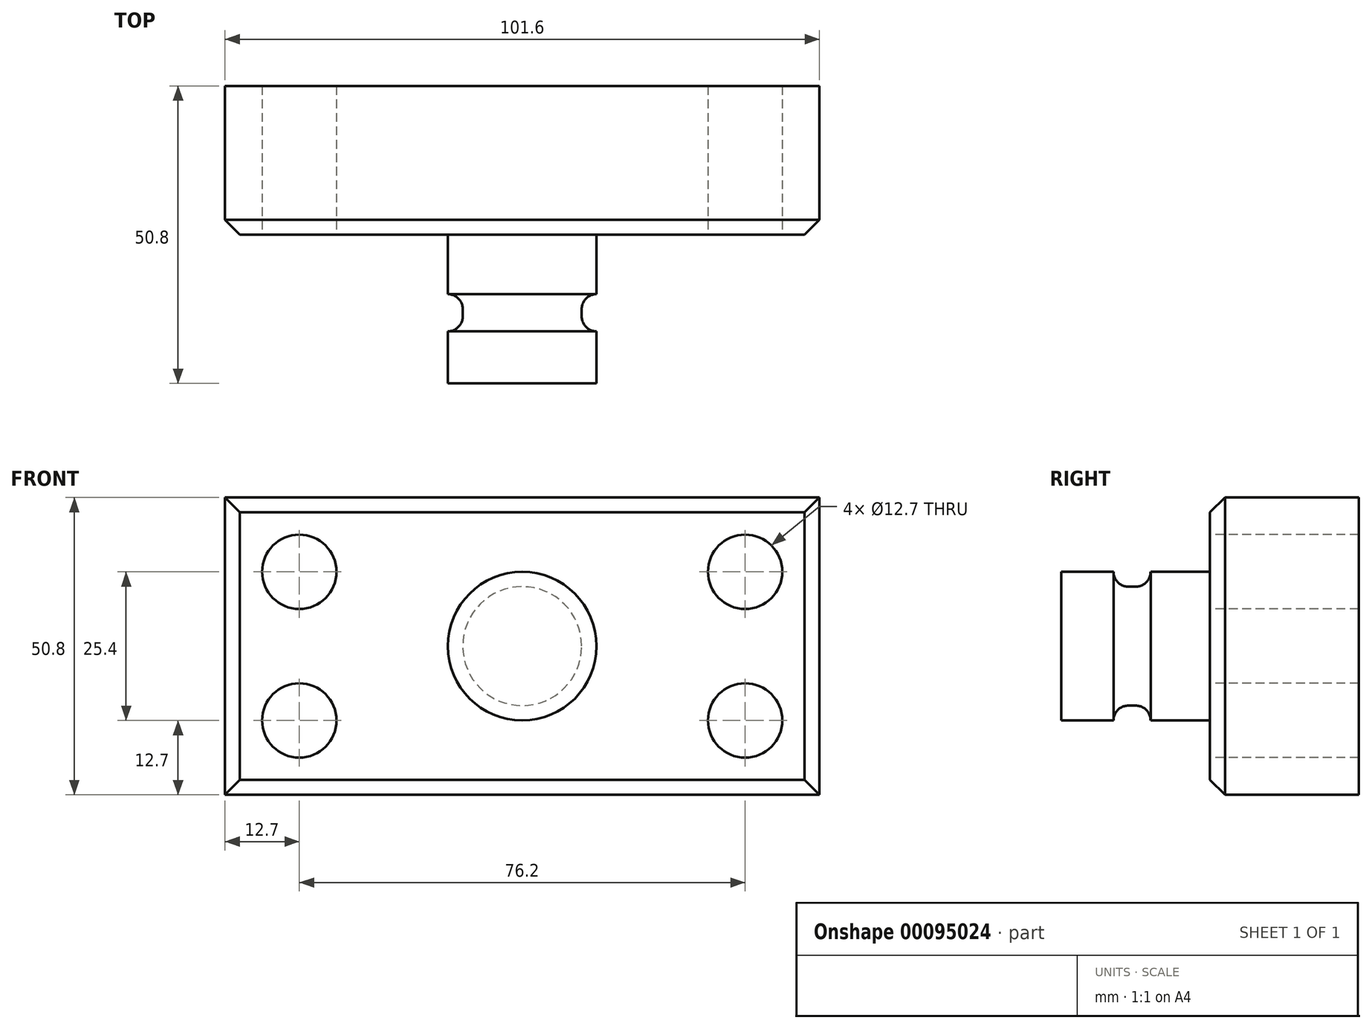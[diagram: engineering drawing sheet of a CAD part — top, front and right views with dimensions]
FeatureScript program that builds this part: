
annotation { "Feature Type Name" : "Feature", "Feature Type Description" : "" }
export const myFeature = defineFeature(function(context is Context, id is Id, definition is map)
    precondition{}
    {
        {
            var Q0;
            Q0=qCreatedBy(makeId("Front.planeOp"),FACE);
            var sketch = newSketch(context, id + "F0", { "sketchPlane" : qUnion([Q0])});
            skLineSegment(sketch, "E0.bottom", {"start": v(-50.8, 25.4) * mm, "end": v(50.8, 25.4) * mm});
            skLineSegment(sketch, "E0.top", {"start": v(-50.8, -25.4) * mm, "end": v(50.8, -25.4) * mm});
            skLineSegment(sketch, "E0.left", {"start": v(-50.8, 25.4) * mm, "end": v(-50.8, -25.4) * mm});
            skLineSegment(sketch, "E0.right", {"start": v(50.8, 25.4) * mm, "end": v(50.8, -25.4) * mm});
            skPoint(sketch, "E0.middle", {"position": v(0, 0) * mm});
            skSolve(sketch);
        }
        {
            var Q0;
            Q0=makeQuery(id+"F0.imprint","IMPRINT",FACE,{"disambiguationData":[TD([[makeQuery(id+"F0.imprint","IMPRINT",EDGE,{"derivedFrom":sQuery(id+"F0.wireOp",EDGE,"E0.bottom")}),-1.0]])]});
            extrude(context, id + "F1", {"entities" : qUnion([Q0]), "depth" : 25.4 * mm});
        }
        {
            var Q0;
            Q0=makeQuery(id+"F1.opExtrude","CAP_FACE",FACE,{"disambiguationData":[OSD([sQuery(id+"F0.wireOp",EDGE,"E0.bottom"),sQuery(id+"F0.wireOp",EDGE,"E0.top"),sQuery(id+"F0.wireOp",EDGE,"E0.left"),sQuery(id+"F0.wireOp",EDGE,"E0.right")])],"isStart":false});
            var sketch = newSketch(context, id + "F2", { "sketchPlane" : qUnion([Q0])});
            skCircle(sketch, "E1", {"center": v(-38.1, 12.7) * mm, "radius": 6.35 * mm});
            skCircle(sketch, "E2", {"center": v(-38.1, -12.7) * mm, "radius": 6.35 * mm});
            skCircle(sketch, "E3", {"center": v(38.1, 12.7) * mm, "radius": 6.35 * mm});
            skCircle(sketch, "E4", {"center": v(38.1, -12.7) * mm, "radius": 6.35 * mm});
            skSolve(sketch);
        }
        {
            var Q0;
            Q0 = qSketchRegion(id + "F2", true);
            extrude(context, id + "F3", {"entities" : qUnion([Q0]), "operationType" : NewBodyOperationType.REMOVE, "endBound" : BoundingType.THROUGH_ALL, "oppositeDirection" : true, "depth" : 25.4 * mm});
        }
        {
            var Q0;
            Q0=qCreatedBy(makeId("Top.planeOp"),FACE);
            var sketch = newSketch(context, id + "F4", { "sketchPlane" : qUnion([Q0])});
            skLineSegment(sketch, "E5.bottom", {"start": v(0, -25.4) * mm, "end": v(-12.7, -25.4) * mm});
            skLineSegment(sketch, "E5.top", {"start": v(0, -50.8) * mm, "end": v(-12.7, -50.8) * mm});
            skLineSegment(sketch, "E5.left", {"start": v(0, -25.4) * mm, "end": v(0, -50.8) * mm});
            skLineSegment(sketch, "E5.right", {"start": v(-12.7, -25.4) * mm, "end": v(-12.7, -50.8) * mm});
            skSolve(sketch);
        }
        {
            var Q0;
            Q0 = qSketchRegion(id + "F4", true);
            var Q1;
            Q1=sQuery(id+"F4.wireOp",EDGE,"E5.left");
            revolve(context, id + "F5", {"operationType" : NewBodyOperationType.ADD, "entities" : qUnion([Q0]), "axis" : qUnion([Q1]), "revolveType" : RevolveType.FULL});
        }
        {
            var Q0;
            Q0=qCreatedBy(makeId("Top.planeOp"),FACE);
            var sketch = newSketch(context, id + "F6", { "sketchPlane" : qUnion([Q0])});
            skLineSegment(sketch, "E6.bottom", {"start": v(-20.32, -41.91) * mm, "end": v(-10.16, -41.91) * mm});
            skLineSegment(sketch, "E6.top", {"start": v(-20.32, -35.56) * mm, "end": v(-10.16, -35.56) * mm});
            skLineSegment(sketch, "E6.left", {"start": v(-20.32, -41.91) * mm, "end": v(-20.32, -35.56) * mm});
            skLineSegment(sketch, "E6.right", {"start": v(-10.16, -41.91) * mm, "end": v(-10.16, -35.56) * mm});
            skLineSegment(sketch, "E7", {"start": v(0, 0) * mm, "end": v(0, -114.82) * mm, "construction": true});
            skSolve(sketch);
        }
        {
            var Q0;
            Q0 = qSketchRegion(id + "F6", true);
            var Q1;
            Q1=sQuery(id+"F6.wireOp",EDGE,"E7");
            revolve(context, id + "F7", {"operationType" : NewBodyOperationType.REMOVE, "entities" : qUnion([Q0]), "axis" : qUnion([Q1]), "revolveType" : RevolveType.FULL, "oppositeDirection" : true});
        }
        {
            var Q0;
            Q0=makeQuery(id+"F5.opRevolve","SWEPT_EDGE",EDGE,{"disambiguationData":[OSD([sQuery(id+"F4.wireOp",EDGE,"E5.bottom"),sQuery(id+"F4.wireOp",EDGE,"E5.right")])]});
            var Q1;
            Q1=makeQuery(id+"F7.boolean.opBoolean","COPY",EDGE,{"derivedFrom":makeQuery(id+"F7.opRevolve","SWEPT_EDGE",EDGE,{"disambiguationData":[OSD([sQuery(id+"F6.wireOp",EDGE,"E6.top"),sQuery(id+"F6.wireOp",EDGE,"E6.right")])]})});
            var Q2;
            Q2=makeQuery(id+"F7.boolean.opBoolean","COPY",FACE,{"derivedFrom":makeQuery(id+"F7.opRevolve","SWEPT_FACE",FACE,{"disambiguationData":[OSD([sQuery(id+"F6.wireOp",EDGE,"E6.right")])]})});
            fillet(context, id + "F8", {"entities" : qUnion([Q0, Q1, Q2]), "radius" : 2.54 * mm, "tangentPropagation" : true, "allowEdgeOverflow" : false});
        }
        {
            var Q0;
            Q0=makeQuery(id+"F1.opExtrude","CAP_EDGE",EDGE,{"disambiguationData":[OSD([sQuery(id+"F0.wireOp",EDGE,"E0.left")])],"isStart":false});
            var Q1;
            Q1=makeQuery(id+"F1.opExtrude","CAP_EDGE",EDGE,{"disambiguationData":[OSD([sQuery(id+"F0.wireOp",EDGE,"E0.bottom")])],"isStart":false});
            var Q2;
            Q2=makeQuery(id+"F1.opExtrude","CAP_EDGE",EDGE,{"disambiguationData":[OSD([sQuery(id+"F0.wireOp",EDGE,"E0.right")])],"isStart":false});
            var Q3;
            Q3=makeQuery(id+"F1.opExtrude","CAP_EDGE",EDGE,{"disambiguationData":[OSD([sQuery(id+"F0.wireOp",EDGE,"E0.top")])],"isStart":false});
            chamfer(context, id + "F9", {"entities" : qUnion([Q0, Q1, Q2, Q3]), "width" : 2.54 * mm, "tangentPropagation" : true});
        }
    });
